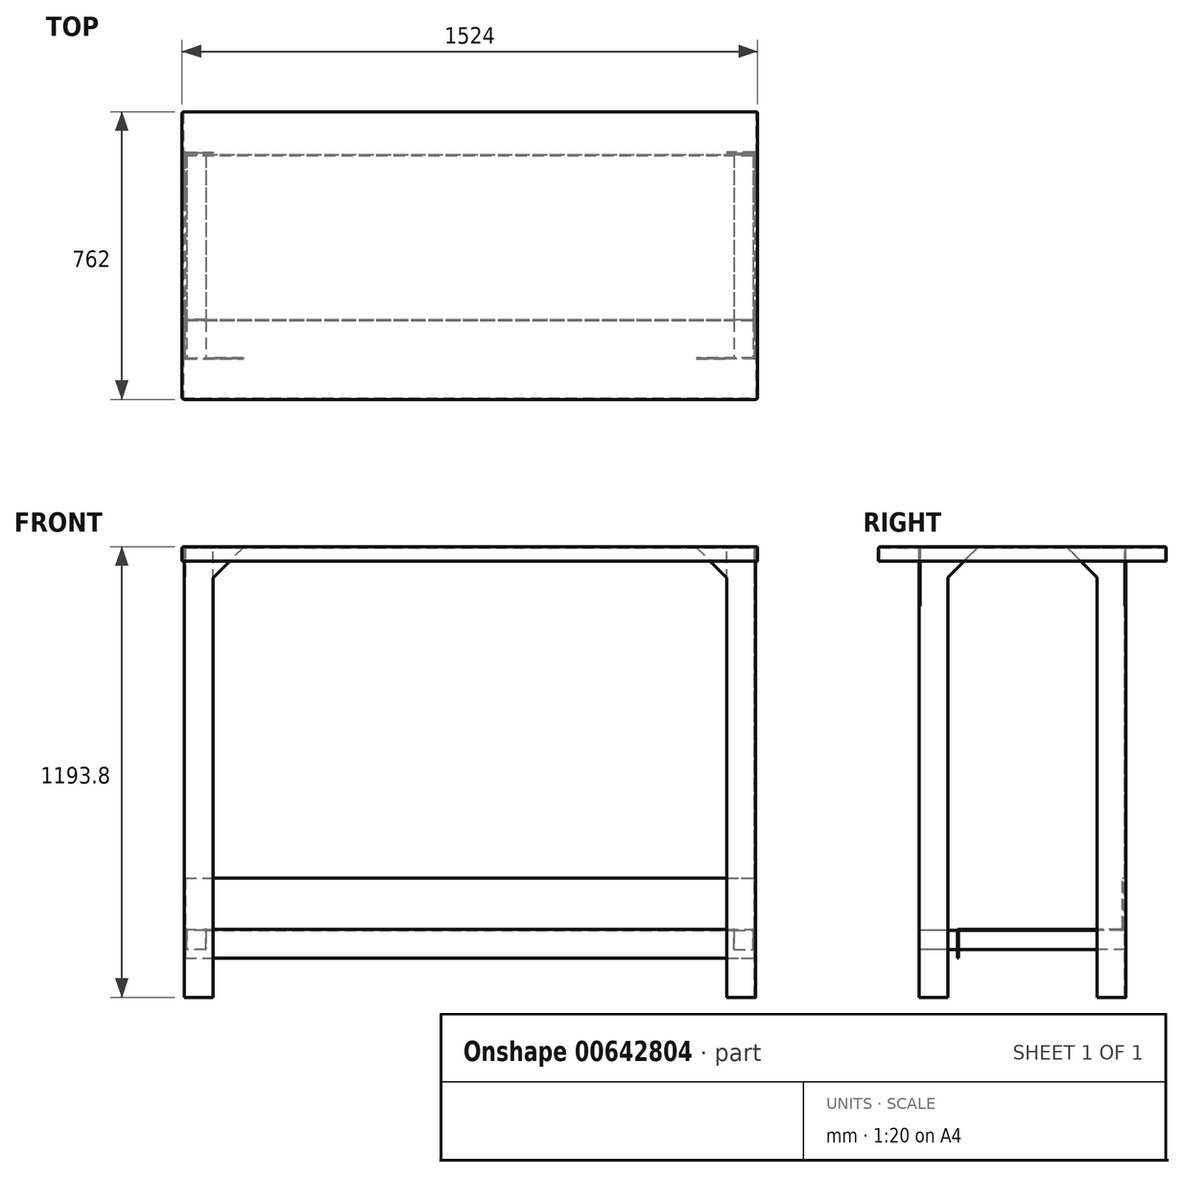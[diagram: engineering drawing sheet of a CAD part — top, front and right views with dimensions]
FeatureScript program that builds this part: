
annotation { "Feature Type Name" : "Feature", "Feature Type Description" : "" }
export const myFeature = defineFeature(function(context is Context, id is Id, definition is map)
    precondition{}
    {
        {
            var Q0;
            Q0=qCreatedBy(makeId("Top.planeOp"),FACE);
            var sketch = newSketch(context, id + "F0", { "sketchPlane" : qUnion([Q0])});
            skLineSegment(sketch, "E0.bottom", {"start": v(762, 381) * mm, "end": v(-762, 381) * mm});
            skLineSegment(sketch, "E0.top", {"start": v(762, -381) * mm, "end": v(-762, -381) * mm});
            skLineSegment(sketch, "E0.left", {"start": v(762, 381) * mm, "end": v(762, -381) * mm});
            skLineSegment(sketch, "E0.right", {"start": v(-762, 381) * mm, "end": v(-762, -381) * mm});
            skPoint(sketch, "E0.middle", {"position": v(0, 0) * mm});
            skSolve(sketch);
        }
        {
            var Q0;
            Q0=makeQuery(id+"F0.imprint","IMPRINT",FACE,{"disambiguationData":[TD([[makeQuery(id+"F0.imprint","IMPRINT",EDGE,{"derivedFrom":sQuery(id+"F0.wireOp",EDGE,"E0.bottom")}),1.0]])]});
            extrude(context, id + "F1", {"entities" : qUnion([Q0]), "depth" : 2.66 * mm, "offsetDistance" : 25.4 * mm});
        }
        {
            var Q0;
            Q0=makeQuery(id+"F1.opExtrude","CAP_FACE",FACE,{"disambiguationData":[OSD([sQuery(id+"F0.wireOp",EDGE,"E0.bottom"),sQuery(id+"F0.wireOp",EDGE,"E0.top"),sQuery(id+"F0.wireOp",EDGE,"E0.left"),sQuery(id+"F0.wireOp",EDGE,"E0.right")])],"isStart":false});
            var sketch = newSketch(context, id + "F2", { "sketchPlane" : qUnion([Q0])});
            skLineSegment(sketch, "E1", {"start": v(-762, -381) * mm, "end": v(762, -381) * mm});
            skLineSegment(sketch, "E2", {"start": v(762, -381) * mm, "end": v(762, 381) * mm});
            skLineSegment(sketch, "E3", {"start": v(762, 381) * mm, "end": v(-762, 381) * mm});
            skLineSegment(sketch, "E4", {"start": v(-762, 381) * mm, "end": v(-762, -381) * mm});
            skLineSegment(sketch, "E5.0", {"start": v(-759.34, 381) * mm, "end": v(-759.34, -381) * mm});
            skLineSegment(sketch, "E6.0", {"start": v(762, 378.34) * mm, "end": v(-762, 378.34) * mm});
            skLineSegment(sketch, "E7.0", {"start": v(759.34, -381) * mm, "end": v(759.34, 381) * mm});
            skLineSegment(sketch, "E8.0", {"start": v(-762, -378.34) * mm, "end": v(762, -378.34) * mm});
            skSolve(sketch);
        }
        {
            var Q0;
            Q0 = qSketchRegion(id + "F2", true);
            extrude(context, id + "F3", {"entities" : qUnion([Q0]), "operationType" : NewBodyOperationType.ADD, "oppositeDirection" : true, "depth" : 38.1 * mm, "offsetDistance" : 25.4 * mm});
        }
        {
            var Q0;
            Q0=makeQuery(id+"F3.boolean.opBoolean","MERGE",EDGE,{"derivedFrom":[makeQuery(id+"F1.opExtrude","SWEPT_EDGE",EDGE,{"disambiguationData":[OSD([sQuery(id+"F0.wireOp",EDGE,"E0.top"),sQuery(id+"F0.wireOp",EDGE,"E0.right")])]}),makeQuery(id+"F3.opExtrude","SWEPT_EDGE",EDGE,{"disambiguationData":[OSD([sQuery(id+"F2.wireOp",EDGE,"E1"),sQuery(id+"F2.wireOp",EDGE,"E4")])]})]});
            var Q1;
            Q1=makeQuery(id+"F3.boolean.opBoolean","MERGE",EDGE,{"derivedFrom":[makeQuery(id+"F1.opExtrude","SWEPT_EDGE",EDGE,{"disambiguationData":[OSD([sQuery(id+"F0.wireOp",EDGE,"E0.top"),sQuery(id+"F0.wireOp",EDGE,"E0.left")])]}),makeQuery(id+"F3.opExtrude","SWEPT_EDGE",EDGE,{"disambiguationData":[OSD([sQuery(id+"F2.wireOp",EDGE,"E1"),sQuery(id+"F2.wireOp",EDGE,"E2")])]})]});
            var Q2;
            Q2=makeQuery(id+"F3.boolean.opBoolean","MERGE",EDGE,{"derivedFrom":[makeQuery(id+"F1.opExtrude","SWEPT_EDGE",EDGE,{"disambiguationData":[OSD([sQuery(id+"F0.wireOp",EDGE,"E0.bottom"),sQuery(id+"F0.wireOp",EDGE,"E0.left")])]}),makeQuery(id+"F3.opExtrude","SWEPT_EDGE",EDGE,{"disambiguationData":[OSD([sQuery(id+"F2.wireOp",EDGE,"E2"),sQuery(id+"F2.wireOp",EDGE,"E3")])]})]});
            var Q3;
            Q3=makeQuery(id+"F3.boolean.opBoolean","MERGE",EDGE,{"derivedFrom":[makeQuery(id+"F1.opExtrude","SWEPT_EDGE",EDGE,{"disambiguationData":[OSD([sQuery(id+"F0.wireOp",EDGE,"E0.bottom"),sQuery(id+"F0.wireOp",EDGE,"E0.right")])]}),makeQuery(id+"F3.opExtrude","SWEPT_EDGE",EDGE,{"disambiguationData":[OSD([sQuery(id+"F2.wireOp",EDGE,"E3"),sQuery(id+"F2.wireOp",EDGE,"E4")])]})]});
            var Q4;
            Q4=makeQuery(id+"F1.opExtrude","CAP_EDGE",EDGE,{"disambiguationData":[OSD([sQuery(id+"F0.wireOp",EDGE,"E0.right")])],"isStart":false});
            var Q5;
            Q5=makeQuery(id+"F1.opExtrude","CAP_EDGE",EDGE,{"disambiguationData":[OSD([sQuery(id+"F0.wireOp",EDGE,"E0.bottom")])],"isStart":false});
            var Q6;
            Q6=makeQuery(id+"F1.opExtrude","CAP_EDGE",EDGE,{"disambiguationData":[OSD([sQuery(id+"F0.wireOp",EDGE,"E0.top")])],"isStart":false});
            var Q7;
            Q7=makeQuery(id+"F1.opExtrude","CAP_EDGE",EDGE,{"disambiguationData":[OSD([sQuery(id+"F0.wireOp",EDGE,"E0.left")])],"isStart":false});
            fillet(context, id + "F4", {"entities" : qUnion([Q0, Q1, Q2, Q3, Q4, Q5, Q6, Q7]), "radius" : 5.3 * mm, "tangentPropagation" : true, "allowEdgeOverflow" : false});
        }
        {
            var Q0;
            Q0=makeQuery(id+"F1.opExtrude","CAP_FACE",FACE,{"disambiguationData":[OSD([sQuery(id+"F0.wireOp",EDGE,"E0.bottom"),sQuery(id+"F0.wireOp",EDGE,"E0.top"),sQuery(id+"F0.wireOp",EDGE,"E0.left"),sQuery(id+"F0.wireOp",EDGE,"E0.right")])],"isStart":false});
            var sketch = newSketch(context, id + "F5", { "sketchPlane" : qUnion([Q0])});
            skLineSegment(sketch, "E9", {"start": v(-756.69, 274.09) * mm, "end": v(-756.69, 197.89) * mm});
            skLineSegment(sketch, "E10", {"start": v(-756.69, 274.09) * mm, "end": v(-680.49, 274.09) * mm});
            skLineSegment(sketch, "E11.0", {"start": v(-754.03, 271.43) * mm, "end": v(-680.49, 271.43) * mm});
            skLineSegment(sketch, "E12.0", {"start": v(-754.03, 271.43) * mm, "end": v(-754.03, 197.89) * mm});
            skLineSegment(sketch, "E13", {"start": v(-680.49, 274.09) * mm, "end": v(-680.49, 271.43) * mm});
            skLineSegment(sketch, "E14", {"start": v(-756.69, 197.89) * mm, "end": v(-754.03, 197.89) * mm});
            skLineSegment(sketch, "E15.MirrorCS", {"start": v(756.69, 197.89) * mm, "end": v(754.03, 197.89) * mm});
            skLineSegment(sketch, "E16.MirrorCS", {"start": v(680.49, 274.09) * mm, "end": v(680.49, 271.43) * mm});
            skLineSegment(sketch, "E17.MirrorCS", {"start": v(754.03, 271.43) * mm, "end": v(754.03, 197.89) * mm});
            skLineSegment(sketch, "E18.MirrorCS", {"start": v(756.69, 274.09) * mm, "end": v(680.49, 274.09) * mm});
            skLineSegment(sketch, "E19.MirrorCS", {"start": v(756.69, 274.09) * mm, "end": v(756.69, 197.89) * mm});
            skLineSegment(sketch, "E20.MirrorCS", {"start": v(754.03, 271.43) * mm, "end": v(680.49, 271.43) * mm});
            skLineSegment(sketch, "E21.MirrorCS", {"start": v(680.49, -274.09) * mm, "end": v(680.49, -271.43) * mm});
            skLineSegment(sketch, "E22.MirrorCS", {"start": v(756.69, -274.09) * mm, "end": v(680.49, -274.09) * mm});
            skLineSegment(sketch, "E23.MirrorCS", {"start": v(756.69, -197.89) * mm, "end": v(754.03, -197.89) * mm});
            skLineSegment(sketch, "E24.MirrorCS", {"start": v(754.03, -271.43) * mm, "end": v(680.49, -271.43) * mm});
            skLineSegment(sketch, "E25.MirrorCS", {"start": v(756.69, -274.09) * mm, "end": v(756.69, -197.89) * mm});
            skLineSegment(sketch, "E26.MirrorCS", {"start": v(754.03, -271.43) * mm, "end": v(754.03, -197.89) * mm});
            skLineSegment(sketch, "E27.MirrorCS", {"start": v(-756.69, -197.89) * mm, "end": v(-754.03, -197.89) * mm});
            skLineSegment(sketch, "E28.MirrorCS", {"start": v(-680.49, -274.09) * mm, "end": v(-680.49, -271.43) * mm});
            skLineSegment(sketch, "E29.MirrorCS", {"start": v(-754.03, -271.43) * mm, "end": v(-754.03, -197.89) * mm});
            skLineSegment(sketch, "E30.MirrorCS", {"start": v(-756.69, -274.09) * mm, "end": v(-756.69, -197.89) * mm});
            skLineSegment(sketch, "E31.MirrorCS", {"start": v(-756.69, -274.09) * mm, "end": v(-680.49, -274.09) * mm});
            skLineSegment(sketch, "E32.MirrorCS", {"start": v(-754.03, -271.43) * mm, "end": v(-680.49, -271.43) * mm});
            skSolve(sketch);
        }
        {
            var Q0;
            Q0 = qSketchRegion(id + "F5", true);
            extrude(context, id + "F6", {"entities" : qUnion([Q0]), "operationType" : NewBodyOperationType.ADD, "oppositeDirection" : true, "depth" : 1193.8 * mm, "offsetDistance" : 25.4 * mm});
        }
        {
            var Q0;
            Q0=makeQuery(id+"F6.opExtrude","SWEPT_EDGE",EDGE,{"disambiguationData":[OSD([sQuery(id+"F0.wireOp",EDGE,"E0.bottom"),sQuery(id+"F0.wireOp",EDGE,"E0.top"),sQuery(id+"F0.wireOp",EDGE,"E0.left"),sQuery(id+"F0.wireOp",EDGE,"E0.right"),sQuery(id+"F5.wireOp",EDGE,"E18.MirrorCS"),sQuery(id+"F5.wireOp",EDGE,"E19.MirrorCS")])]});
            var Q1;
            Q1=makeQuery(id+"F6.opExtrude","SWEPT_EDGE",EDGE,{"disambiguationData":[OSD([sQuery(id+"F0.wireOp",EDGE,"E0.bottom"),sQuery(id+"F0.wireOp",EDGE,"E0.top"),sQuery(id+"F0.wireOp",EDGE,"E0.left"),sQuery(id+"F0.wireOp",EDGE,"E0.right"),sQuery(id+"F5.wireOp",EDGE,"E9"),sQuery(id+"F5.wireOp",EDGE,"E10")])]});
            var Q2;
            Q2=makeQuery(id+"F6.opExtrude","SWEPT_EDGE",EDGE,{"disambiguationData":[OSD([sQuery(id+"F0.wireOp",EDGE,"E0.bottom"),sQuery(id+"F0.wireOp",EDGE,"E0.top"),sQuery(id+"F0.wireOp",EDGE,"E0.left"),sQuery(id+"F0.wireOp",EDGE,"E0.right"),sQuery(id+"F5.wireOp",EDGE,"E30.MirrorCS"),sQuery(id+"F5.wireOp",EDGE,"E31.MirrorCS")])]});
            var Q3;
            Q3=makeQuery(id+"F6.opExtrude","SWEPT_EDGE",EDGE,{"disambiguationData":[OSD([sQuery(id+"F0.wireOp",EDGE,"E0.bottom"),sQuery(id+"F0.wireOp",EDGE,"E0.top"),sQuery(id+"F0.wireOp",EDGE,"E0.left"),sQuery(id+"F0.wireOp",EDGE,"E0.right"),sQuery(id+"F5.wireOp",EDGE,"E22.MirrorCS"),sQuery(id+"F5.wireOp",EDGE,"E25.MirrorCS")])]});
            fillet(context, id + "F7", {"entities" : qUnion([Q0, Q1, Q2, Q3]), "radius" : 4 * mm, "tangentPropagation" : true, "allowEdgeOverflow" : false});
        }
        {
            var Q0;
            Q0=makeQuery(id+"F6.opExtrude","SWEPT_EDGE",EDGE,{"disambiguationData":[OSD([sQuery(id+"F5.wireOp",EDGE,"E29.MirrorCS"),sQuery(id+"F5.wireOp",EDGE,"E32.MirrorCS")])]});
            var Q1;
            Q1=makeQuery(id+"F6.opExtrude","SWEPT_EDGE",EDGE,{"disambiguationData":[OSD([sQuery(id+"F5.wireOp",EDGE,"E11.0"),sQuery(id+"F5.wireOp",EDGE,"E12.0")])]});
            var Q2;
            Q2=makeQuery(id+"F6.opExtrude","SWEPT_EDGE",EDGE,{"disambiguationData":[OSD([sQuery(id+"F5.wireOp",EDGE,"E24.MirrorCS"),sQuery(id+"F5.wireOp",EDGE,"E26.MirrorCS")])]});
            var Q3;
            Q3=makeQuery(id+"F6.opExtrude","SWEPT_EDGE",EDGE,{"disambiguationData":[OSD([sQuery(id+"F5.wireOp",EDGE,"E17.MirrorCS"),sQuery(id+"F5.wireOp",EDGE,"E20.MirrorCS")])]});
            fillet(context, id + "F8", {"entities" : qUnion([Q0, Q1, Q2, Q3]), "radius" : 4 * mm, "tangentPropagation" : true, "allowEdgeOverflow" : false});
        }
        {
            var Q0;
            Q0=makeQuery(id+"F6.opExtrude","SWEPT_FACE",FACE,{"disambiguationData":[OSD([sQuery(id+"F5.wireOp",EDGE,"E32.MirrorCS")])]});
            var sketch = newSketch(context, id + "F9", { "sketchPlane" : qUnion([Q0])});
            skLineSegment(sketch, "E33.bottom", {"start": v(750.04, -1064.14) * mm, "end": v(699.24, -1064.14) * mm});
            skLineSegment(sketch, "E33.top", {"start": v(750.04, -1013.34) * mm, "end": v(699.24, -1013.34) * mm});
            skLineSegment(sketch, "E33.left", {"start": v(750.04, -1064.14) * mm, "end": v(750.04, -1013.34) * mm});
            skLineSegment(sketch, "E33.right", {"start": v(699.24, -1064.14) * mm, "end": v(699.24, -1013.34) * mm});
            skLineSegment(sketch, "E34.MirrorCS", {"start": v(-750.04, -1064.14) * mm, "end": v(-699.24, -1064.14) * mm});
            skLineSegment(sketch, "E35.MirrorCS", {"start": v(-750.04, -1064.14) * mm, "end": v(-750.04, -1013.34) * mm});
            skLineSegment(sketch, "E36.MirrorCS", {"start": v(-750.04, -1013.34) * mm, "end": v(-699.24, -1013.34) * mm});
            skLineSegment(sketch, "E37.MirrorCS", {"start": v(-699.24, -1064.14) * mm, "end": v(-699.24, -1013.34) * mm});
            skSolve(sketch);
        }
        {
            var Q0;
            Q0 = qSketchRegion(id + "F9", true);
            var Q1;
            Q1=makeQuery(id+"F6.opExtrude","SWEPT_FACE",FACE,{"disambiguationData":[OSD([sQuery(id+"F5.wireOp",EDGE,"E11.0")])]});
            extrude(context, id + "F10", {"entities" : qUnion([Q0]), "operationType" : NewBodyOperationType.ADD, "endBound" : BoundingType.UP_TO_SURFACE, "depth" : 25.4 * mm, "endBoundEntityFace" : qUnion([Q1]), "offsetDistance" : 25.4 * mm});
        }
        {
            var Q0;
            Q0=makeQuery(id+"F6.opExtrude","SWEPT_FACE",FACE,{"disambiguationData":[OSD([sQuery(id+"F5.wireOp",EDGE,"E17.MirrorCS")])]});
            var sketch = newSketch(context, id + "F11", { "sketchPlane" : qUnion([Q0])});
            skLineSegment(sketch, "E38.bottom", {"start": v(-267.44, -1013.34) * mm, "end": v(169.83, -1013.34) * mm});
            skLineSegment(sketch, "E38.top", {"start": v(-264.79, -1010.69) * mm, "end": v(172.49, -1010.69) * mm});
            skLineSegment(sketch, "E38.right", {"start": v(172.49, -1086.89) * mm, "end": v(172.49, -1010.69) * mm});
            skLineSegment(sketch, "E39", {"start": v(-264.79, -1010.69) * mm, "end": v(-264.79, -876) * mm});
            skLineSegment(sketch, "E40", {"start": v(-264.79, -876) * mm, "end": v(-267.44, -876) * mm});
            skLineSegment(sketch, "E41", {"start": v(-267.44, -876) * mm, "end": v(-267.44, -1013.34) * mm});
            skLineSegment(sketch, "E42", {"start": v(169.83, -1013.34) * mm, "end": v(169.83, -1086.89) * mm});
            skLineSegment(sketch, "E43", {"start": v(169.83, -1086.89) * mm, "end": v(172.49, -1086.89) * mm});
            skSolve(sketch);
        }
        {
            var Q0;
            Q0 = qSketchRegion(id + "F11", true);
            var Q1;
            Q1=makeQuery(id+"F6.opExtrude","SWEPT_FACE",FACE,{"disambiguationData":[OSD([sQuery(id+"F5.wireOp",EDGE,"E12.0")])]});
            extrude(context, id + "F12", {"entities" : qUnion([Q0]), "operationType" : NewBodyOperationType.ADD, "endBound" : BoundingType.UP_TO_SURFACE, "depth" : 25.4 * mm, "endBoundEntityFace" : qUnion([Q1]), "offsetDistance" : 25.4 * mm});
        }
        {
            var Q0;
            Q0=makeQuery(id+"F12.opExtrude","SWEPT_EDGE",EDGE,{"disambiguationData":[OSD([sQuery(id+"F11.wireOp",EDGE,"E38.top"),sQuery(id+"F11.wireOp",EDGE,"E39")])]});
            var Q1;
            {var subQ0=sQuery(id+"F11.wireOp",EDGE,"E38.bottom");var subQ1=makeQuery(id+"F12.opExtrude","SWEPT_FACE",FACE,{"disambiguationData":[OSD([subQ0])]});var subQ2=sQuery(id+"F11.wireOp",EDGE,"E41");var subQ3=makeQuery(id+"F12.opExtrude","SWEPT_FACE",FACE,{"disambiguationData":[OSD([subQ2])]});Q1=makeQuery(id+"F12.boolean.opBoolean","SPLIT",EDGE,{"disambiguationData":[topologyDisambiguationEdgeConnected([subQ1,subQ3]),TD([makeQuery(id+"F10.opExtrude","SWEPT_FACE",FACE,{"disambiguationData":[OSD([sQuery(id+"F9.wireOp",EDGE,"E33.right")])]})])],"derivedFrom":makeQuery(id+"F12.opExtrude","SWEPT_EDGE",EDGE,{"disambiguationData":[OSD([sQuery(id+"F5.wireOp",EDGE,"E17.MirrorCS"),sQuery(id+"F5.wireOp",EDGE,"E20.MirrorCS"),subQ0,subQ2])]})});}
            var Q2;
            Q2=makeQuery(id+"F12.opExtrude","SWEPT_EDGE",EDGE,{"disambiguationData":[OSD([sQuery(id+"F11.wireOp",EDGE,"E38.top"),sQuery(id+"F11.wireOp",EDGE,"E38.right")])]});
            var Q3;
            {var subQ0=sQuery(id+"F11.wireOp",EDGE,"E38.bottom");var subQ1=sQuery(id+"F11.wireOp",EDGE,"E42");Q3=makeQuery(id+"F12.boolean.opBoolean","SPLIT",EDGE,{"disambiguationData":[TD([makeQuery(id+"F10.opExtrude","SWEPT_FACE",FACE,{"disambiguationData":[OSD([sQuery(id+"F9.wireOp",EDGE,"E33.right")])]})])],"derivedFrom":makeQuery(id+"F12.opExtrude","SWEPT_EDGE",EDGE,{"disambiguationData":[OSD([subQ0,subQ1])]})});}
            fillet(context, id + "F13", {"entities" : qUnion([Q0, Q1, Q2, Q3]), "radius" : 5.08 * mm, "tangentPropagation" : true, "allowEdgeOverflow" : false});
        }
        {
            var Q0;
            Q0=makeQuery(id+"F6.opExtrude","SWEPT_FACE",FACE,{"disambiguationData":[OSD([sQuery(id+"F5.wireOp",EDGE,"E31.MirrorCS")])]});
            var sketch = newSketch(context, id + "F14", { "sketchPlane" : qUnion([Q0])});
            skLineSegment(sketch, "E44", {"start": v(-752.7, 0) * mm, "end": v(-600.3, 0) * mm});
            skLineSegment(sketch, "E45", {"start": v(-600.3, 0) * mm, "end": v(-752.7, -152.4) * mm});
            skLineSegment(sketch, "E46", {"start": v(-752.7, -152.4) * mm, "end": v(-752.7, 0) * mm});
            skLineSegment(sketch, "E47.MirrorCS", {"start": v(600.3, 0) * mm, "end": v(752.7, -152.4) * mm});
            skLineSegment(sketch, "E48.MirrorCS", {"start": v(752.7, 0) * mm, "end": v(600.3, 0) * mm});
            skLineSegment(sketch, "E49.MirrorCS", {"start": v(752.7, -152.4) * mm, "end": v(752.7, 0) * mm});
            skSolve(sketch);
        }
        {
            var Q0;
            Q0 = qSketchRegion(id + "F14", true);
            extrude(context, id + "F15", {"entities" : qUnion([Q0]), "operationType" : NewBodyOperationType.ADD, "oppositeDirection" : true, "depth" : 2.66 * mm, "offsetDistance" : 25.4 * mm});
        }
        {
            var Q0;
            Q0=makeQuery(id+"F6.opExtrude","SWEPT_FACE",FACE,{"disambiguationData":[OSD([sQuery(id+"F5.wireOp",EDGE,"E25.MirrorCS")])]});
            var sketch = newSketch(context, id + "F16", { "sketchPlane" : qUnion([Q0])});
            skLineSegment(sketch, "E50", {"start": v(-119.03, 0) * mm, "end": v(-271.43, 0) * mm});
            skLineSegment(sketch, "E51", {"start": v(-271.43, 0) * mm, "end": v(-271.43, -152.4) * mm});
            skLineSegment(sketch, "E52", {"start": v(-271.43, -152.4) * mm, "end": v(-119.03, 0) * mm});
            skLineSegment(sketch, "E53.MirrorCS", {"start": v(271.43, -152.4) * mm, "end": v(119.03, 0) * mm});
            skLineSegment(sketch, "E54.MirrorCS", {"start": v(119.03, 0) * mm, "end": v(271.43, 0) * mm});
            skLineSegment(sketch, "E55.MirrorCS", {"start": v(271.43, 0) * mm, "end": v(271.43, -152.4) * mm});
            skSolve(sketch);
        }
        {
            var Q0;
            Q0 = qSketchRegion(id + "F16", true);
            extrude(context, id + "F17", {"entities" : qUnion([Q0]), "operationType" : NewBodyOperationType.ADD, "oppositeDirection" : true, "depth" : 2.66 * mm, "offsetDistance" : 25.4 * mm});
        }
        {
            var Q0;
            Q0=makeQuery(id+"F6.opExtrude","SWEPT_FACE",FACE,{"disambiguationData":[OSD([sQuery(id+"F5.wireOp",EDGE,"E9")])]});
            var sketch = newSketch(context, id + "F18", { "sketchPlane" : qUnion([Q0])});
            skLineSegment(sketch, "E56", {"start": v(-119.03, 0) * mm, "end": v(-271.43, -152.4) * mm});
            skLineSegment(sketch, "E57", {"start": v(-271.43, -152.4) * mm, "end": v(-271.43, 0) * mm});
            skLineSegment(sketch, "E58", {"start": v(-271.43, 0) * mm, "end": v(-119.03, 0) * mm});
            skLineSegment(sketch, "E59.MirrorCS", {"start": v(271.43, 0) * mm, "end": v(119.03, 0) * mm});
            skLineSegment(sketch, "E60.MirrorCS", {"start": v(271.43, -152.4) * mm, "end": v(271.43, 0) * mm});
            skLineSegment(sketch, "E61.MirrorCS", {"start": v(119.03, 0) * mm, "end": v(271.43, -152.4) * mm});
            skSolve(sketch);
        }
        {
            var Q0;
            Q0 = qSketchRegion(id + "F18", true);
            extrude(context, id + "F19", {"entities" : qUnion([Q0]), "operationType" : NewBodyOperationType.ADD, "oppositeDirection" : true, "depth" : 2.66 * mm, "offsetDistance" : 25.4 * mm});
        }
    });
